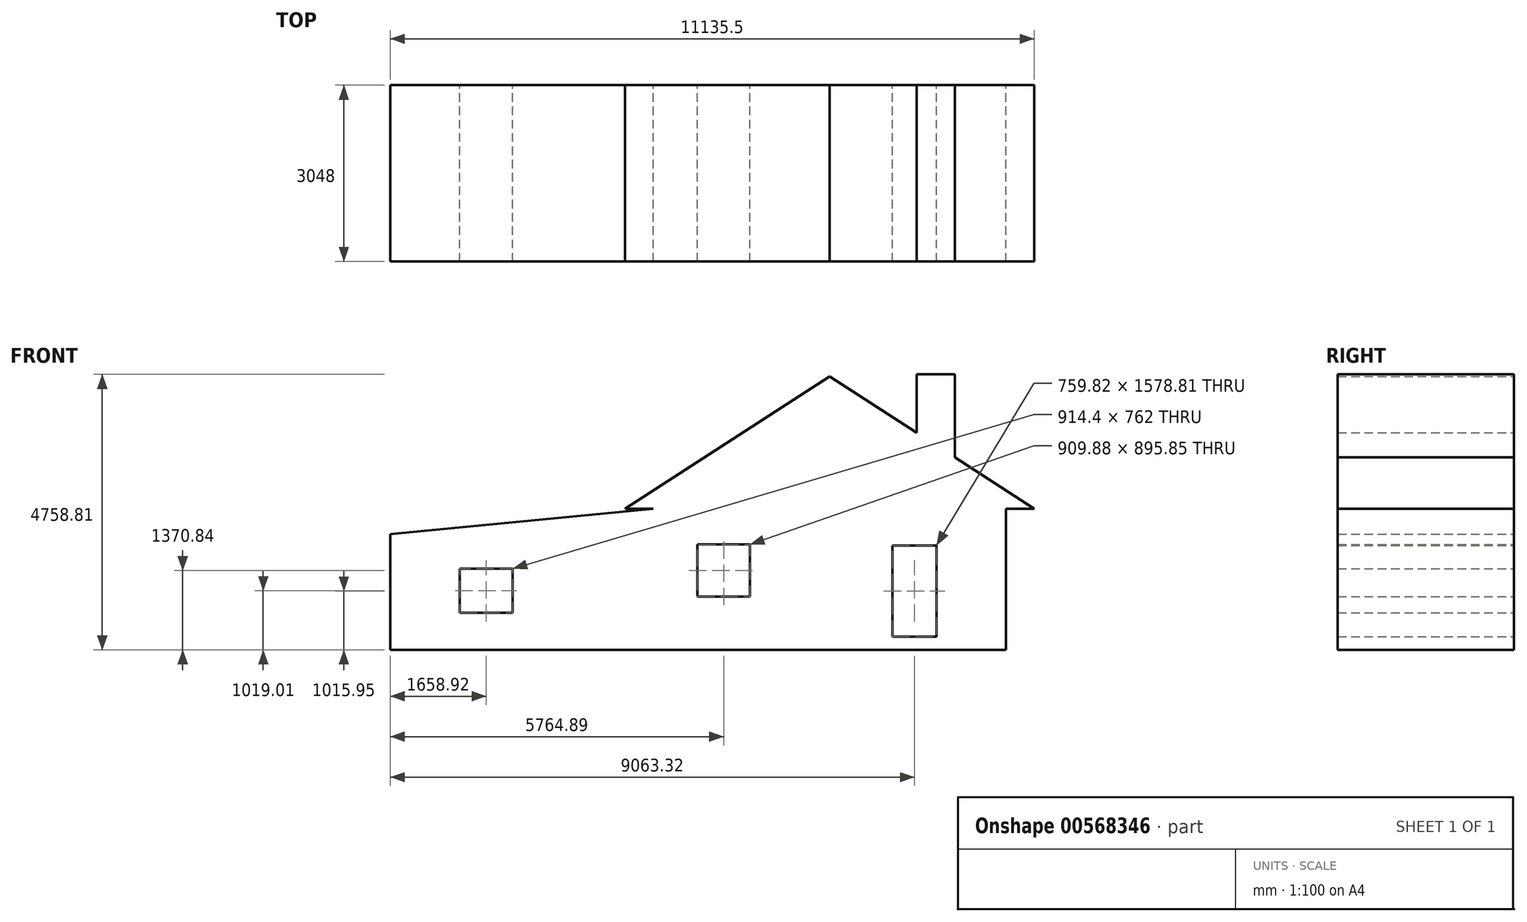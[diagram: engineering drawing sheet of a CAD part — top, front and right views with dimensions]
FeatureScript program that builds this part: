
annotation { "Feature Type Name" : "Feature", "Feature Type Description" : "" }
export const myFeature = defineFeature(function(context is Context, id is Id, definition is map)
    precondition{}
    {
        {
            var Q0;
            Q0=qCreatedBy(makeId("Front.planeOp"),FACE);
            var sketch = newSketch(context, id + "F0", { "sketchPlane" : qUnion([Q0])});
            skLineSegment(sketch, "E0", {"start": v(0, 0) * mm, "end": v(-3048, 0) * mm});
            skLineSegment(sketch, "E1", {"start": v(0, 0) * mm, "end": v(3048, 0) * mm});
            skLineSegment(sketch, "E2", {"start": v(0, 0) * mm, "end": v(0, 1981.2) * mm});
            skLineSegment(sketch, "E3", {"start": v(0, 1981.2) * mm, "end": v(-3048, 0) * mm});
            skLineSegment(sketch, "E4", {"start": v(0, 1981.2) * mm, "end": v(3048, 0) * mm});
            skLineSegment(sketch, "E5", {"start": v(0, 1981.2) * mm, "end": v(0, 2286) * mm});
            skLineSegment(sketch, "E6", {"start": v(0, 2286) * mm, "end": v(-3539.34, 0) * mm});
            skLineSegment(sketch, "E7", {"start": v(-3539.34, 0) * mm, "end": v(-3048, 0) * mm});
            skLineSegment(sketch, "E8", {"start": v(3048, 0) * mm, "end": v(3539.34, 0) * mm});
            skLineSegment(sketch, "E9", {"start": v(3539.34, 0) * mm, "end": v(0, 2286) * mm});
            skLineSegment(sketch, "E10", {"start": v(3048, 0) * mm, "end": v(3048, -2438.4) * mm});
            skLineSegment(sketch, "E11", {"start": v(-3048, 0) * mm, "end": v(-3048, -2438.4) * mm});
            skLineSegment(sketch, "E12", {"start": v(-3048, -2438.4) * mm, "end": v(3278.2, -2438.4) * mm});
            skLineSegment(sketch, "E13", {"start": v(-7596.13, -420.12) * mm, "end": v(-7596.13, -2438.4) * mm});
            skLineSegment(sketch, "E14", {"start": v(-7596.13, -2438.4) * mm, "end": v(-3048, -2438.4) * mm});
            skLineSegment(sketch, "E15", {"start": v(-3048, 0) * mm, "end": v(-7596.13, -439.93) * mm});
            skLineSegment(sketch, "E16", {"start": v(-3048, -265.28) * mm, "end": v(-7596.13, -705.21) * mm});
            skLineSegment(sketch, "E17", {"start": v(-7596.13, -2211.85) * mm, "end": v(3048, -2211.85) * mm});
            skLineSegment(sketch, "E18", {"start": v(3048, -2211.85) * mm, "end": v(3048, -2438.4) * mm});
            skLineSegment(sketch, "E19", {"start": v(-7596.13, -2211.85) * mm, "end": v(-7596.13, -2438.4) * mm});
            skLineSegment(sketch, "E20", {"start": v(1163.45, -2211.85) * mm, "end": v(1163.45, -687.85) * mm});
            skLineSegment(sketch, "E21", {"start": v(1163.45, -687.85) * mm, "end": v(1773.05, -687.85) * mm});
            skLineSegment(sketch, "E22", {"start": v(1773.05, -687.85) * mm, "end": v(1773.05, -2211.85) * mm});
            skLineSegment(sketch, "E23", {"start": v(-2214.75, -689.33) * mm, "end": v(-2214.75, -1451.33) * mm});
            skLineSegment(sketch, "E24", {"start": v(-2214.75, -1451.33) * mm, "end": v(-1452.75, -1451.33) * mm});
            skLineSegment(sketch, "E25", {"start": v(-1452.75, -1451.33) * mm, "end": v(-1452.75, -689.33) * mm});
            skLineSegment(sketch, "E26", {"start": v(-1452.75, -689.33) * mm, "end": v(-2214.75, -689.33) * mm});
            skLineSegment(sketch, "E27", {"start": v(-6394.4, -1038.39) * mm, "end": v(-6394.4, -1800.39) * mm});
            skLineSegment(sketch, "E28", {"start": v(-6394.4, -1800.39) * mm, "end": v(-5480, -1800.39) * mm});
            skLineSegment(sketch, "E29", {"start": v(-5480, -1800.39) * mm, "end": v(-5480, -1038.39) * mm});
            skLineSegment(sketch, "E30", {"start": v(-5480, -1038.39) * mm, "end": v(-6394.4, -1038.39) * mm});
            skLineSegment(sketch, "E31", {"start": v(-2286.18, -1515.48) * mm, "end": v(-2286.18, -619.63) * mm});
            skLineSegment(sketch, "E32", {"start": v(-2286.18, -619.63) * mm, "end": v(-1376.3, -619.63) * mm});
            skLineSegment(sketch, "E33", {"start": v(-1376.3, -619.63) * mm, "end": v(-1376.3, -1515.48) * mm});
            skLineSegment(sketch, "E34", {"start": v(-1376.3, -1515.48) * mm, "end": v(-2286.18, -1515.48) * mm});
            skLineSegment(sketch, "E35", {"start": v(-6467.28, -1874.69) * mm, "end": v(-6467.28, -962.14) * mm});
            skLineSegment(sketch, "E36", {"start": v(-6467.28, -962.14) * mm, "end": v(-5409.28, -962.14) * mm});
            skLineSegment(sketch, "E37", {"start": v(-5405.67, -953.87) * mm, "end": v(-5405.67, -1877.3) * mm});
            skLineSegment(sketch, "E38", {"start": v(-5405.67, -1877.3) * mm, "end": v(-6467.28, -1877.3) * mm});
            skLineSegment(sketch, "E39", {"start": v(1087.28, -2211.85) * mm, "end": v(1087.28, -633.05) * mm});
            skLineSegment(sketch, "E40", {"start": v(1087.28, -633.05) * mm, "end": v(1847.1, -633.05) * mm});
            skLineSegment(sketch, "E41", {"start": v(1847.1, -633.05) * mm, "end": v(1847.1, -2211.85) * mm});
            skLineSegment(sketch, "E42", {"start": v(1503.23, 1315.09) * mm, "end": v(1503.23, 2320.4) * mm});
            skLineSegment(sketch, "E43", {"start": v(1503.23, 2320.4) * mm, "end": v(2163.16, 2320.4) * mm});
            skLineSegment(sketch, "E44", {"start": v(2163.16, 2320.4) * mm, "end": v(2163.16, 888.85) * mm});
            skSolve(sketch);
        }
        {
            var Q0;
            Q0 = qSketchRegion(id + "F0", true);
            extrude(context, id + "F1", {"entities" : qUnion([Q0]), "depth" : 3048 * mm, "offsetDistance" : 30.48 * mm});
        }
    });
